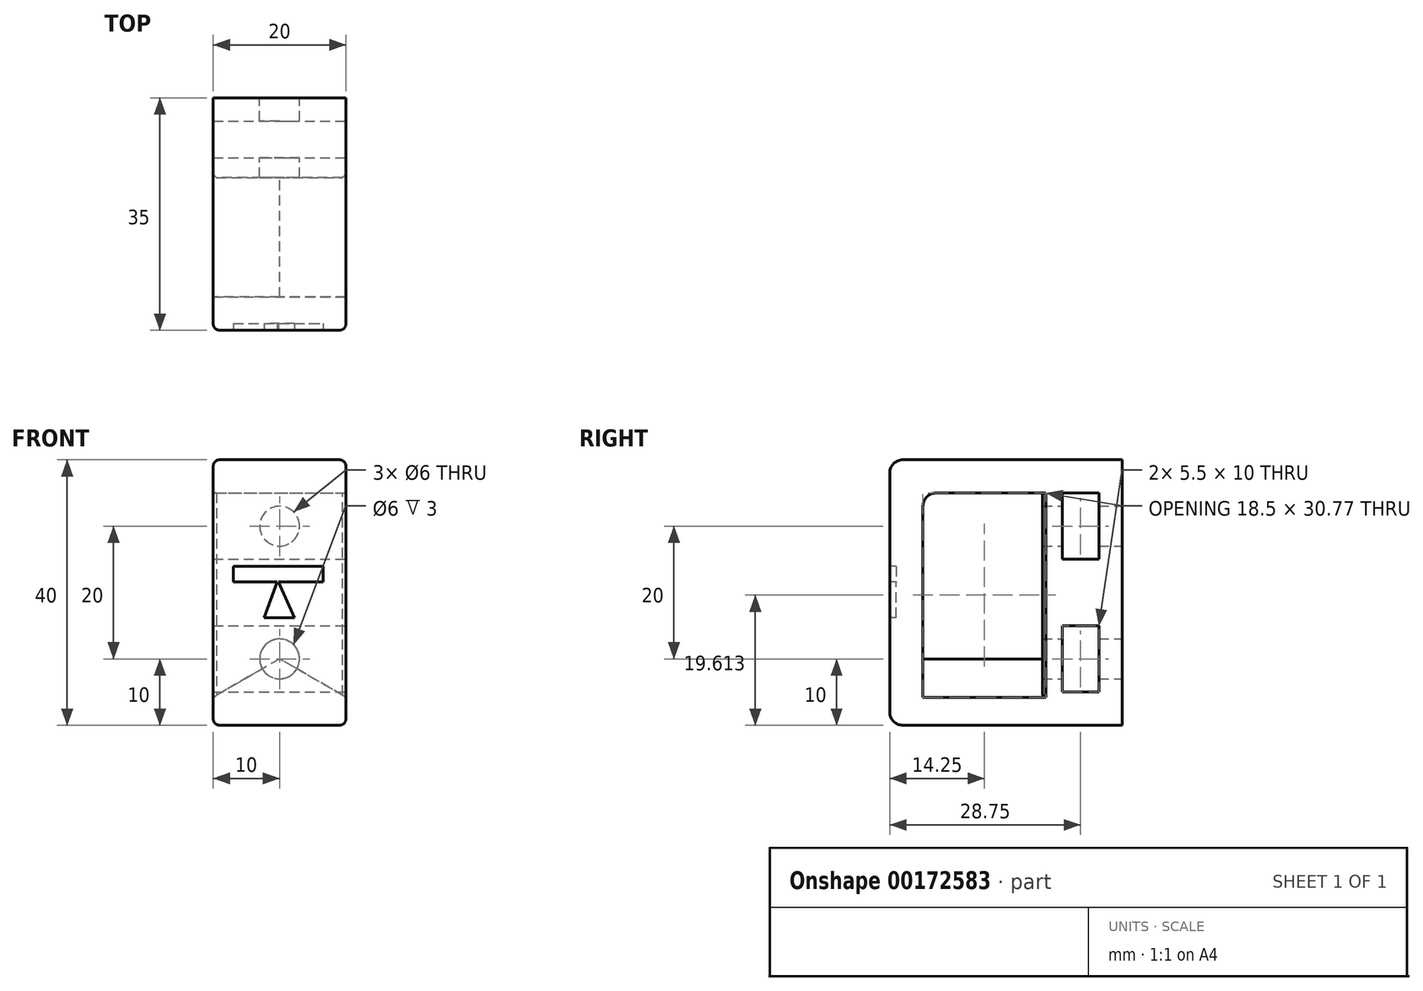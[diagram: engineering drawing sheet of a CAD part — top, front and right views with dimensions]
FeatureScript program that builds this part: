
annotation { "Feature Type Name" : "Feature", "Feature Type Description" : "" }
export const myFeature = defineFeature(function(context is Context, id is Id, definition is map)
    precondition{}
    {
        {
            var Q0;
            Q0=qCreatedBy(makeId("Front.planeOp"),FACE);
            var sketch = newSketch(context, id + "F0", { "sketchPlane" : qUnion([Q0])});
            skLineSegment(sketch, "E0.bottom", {"start": v(0, 0) * mm, "end": v(20, 0) * mm});
            skLineSegment(sketch, "E0.top", {"start": v(0, 40) * mm, "end": v(20, 40) * mm});
            skLineSegment(sketch, "E0.left", {"start": v(0, 0) * mm, "end": v(0, 40) * mm});
            skLineSegment(sketch, "E0.right", {"start": v(20, 0) * mm, "end": v(20, 40) * mm});
            skSolve(sketch);
        }
        {
            var Q0;
            Q0=qSketchRegion(id+"F0",true);
            extrude(context, id + "F1", {"entities" : qUnion([Q0]), "depth" : 12 * mm});
        }
        {
            var Q0;
            Q0=makeQuery(id+"F1.opExtrude","CAP_FACE",FACE,{"disambiguationData":[OSD([sQuery(id+"F0.wireOp",EDGE,"E0.bottom"),sQuery(id+"F0.wireOp",EDGE,"E0.top"),sQuery(id+"F0.wireOp",EDGE,"E0.left"),sQuery(id+"F0.wireOp",EDGE,"E0.right")])],"isStart":true});
            var sketch = newSketch(context, id + "F2", { "sketchPlane" : qUnion([Q0])});
            skCircle(sketch, "E1", {"center": v(-10, 30) * mm, "radius": 3 * mm});
            skPoint(sketch, "E1.centerSnap0", {"position": v(-10, 40) * mm});
            skCircle(sketch, "E2", {"center": v(-10, 10) * mm, "radius": 3 * mm});
            skSolve(sketch);
        }
        {
            var Q0;
            Q0=qSketchRegion(id+"F2",true);
            var Q1;
            Q1=makeQuery(id+"F1.opExtrude","CAP_FACE",FACE,{"disambiguationData":[OSD([sQuery(id+"F0.wireOp",EDGE,"E0.bottom"),sQuery(id+"F0.wireOp",EDGE,"E0.top"),sQuery(id+"F0.wireOp",EDGE,"E0.left"),sQuery(id+"F0.wireOp",EDGE,"E0.right")])],"isStart":false});
            extrude(context, id + "F3", {"entities" : qUnion([Q0]), "operationType" : NewBodyOperationType.REMOVE, "endBound" : BoundingType.UP_TO_SURFACE, "oppositeDirection" : true, "endBoundEntityFace" : qUnion([Q1]), "depth" : 25 * mm});
        }
        {
            var Q0;
            Q0=makeQuery(id+"F1.opExtrude","CAP_FACE",FACE,{"disambiguationData":[OSD([sQuery(id+"F0.wireOp",EDGE,"E0.bottom"),sQuery(id+"F0.wireOp",EDGE,"E0.top"),sQuery(id+"F0.wireOp",EDGE,"E0.left"),sQuery(id+"F0.wireOp",EDGE,"E0.right")])],"isStart":false});
            var sketch = newSketch(context, id + "F4", { "sketchPlane" : qUnion([Q0])});
            skLineSegment(sketch, "E3", {"start": v(0, 0) * mm, "end": v(20, 0) * mm});
            skLineSegment(sketch, "E4", {"start": v(20, 0) * mm, "end": v(20, 4.23) * mm});
            skLineSegment(sketch, "E5", {"start": v(20, 4.23) * mm, "end": v(10, 10) * mm});
            skPoint(sketch, "E5.endSnap0", {"position": v(10, 0) * mm});
            skLineSegment(sketch, "E6", {"start": v(10, 10) * mm, "end": v(0, 4.23) * mm});
            skLineSegment(sketch, "E7", {"start": v(0, 4.23) * mm, "end": v(0, 0) * mm});
            skSolve(sketch);
        }
        {
            var Q0;
            Q0 = qSketchRegion(id + "F4", true);
            extrude(context, id + "F5", {"entities" : qUnion([Q0]), "operationType" : NewBodyOperationType.ADD, "depth" : 23 * mm});
        }
        {
            var Q0;
            Q0=makeQuery(id+"F5.boolean.opBoolean","MERGE",FACE,{"derivedFrom":[makeQuery(id+"F1.opExtrude","SWEPT_FACE",FACE,{"disambiguationData":[OSD([sQuery(id+"F0.wireOp",EDGE,"E0.right")])]}),makeQuery(id+"F5.opExtrude","SWEPT_FACE",FACE,{"disambiguationData":[OSD([sQuery(id+"F4.wireOp",EDGE,"E4")])]})]});
            var sketch = newSketch(context, id + "F6", { "sketchPlane" : qUnion([Q0])});
            skLineSegment(sketch, "E8", {"start": v(-35, 0) * mm, "end": v(-35, 40) * mm});
            skLineSegment(sketch, "E9", {"start": v(-35, 40) * mm, "end": v(-12, 40) * mm});
            skLineSegment(sketch, "E10", {"start": v(-12, 40) * mm, "end": v(-12, 35) * mm});
            skLineSegment(sketch, "E11", {"start": v(-12, 35) * mm, "end": v(-30, 35) * mm});
            skLineSegment(sketch, "E12", {"start": v(-30, 35) * mm, "end": v(-30, 0) * mm});
            skLineSegment(sketch, "E13", {"start": v(-30, 0) * mm, "end": v(-35, 0) * mm});
            skSolve(sketch);
        }
        {
            var Q0;
            {var subQ1=sQuery(id+"F6.wireOp",EDGE,"E9");Q0=makeQuery(id+"F6.imprint","IMPRINT",FACE,{"disambiguationData":[TD([[makeQuery(id+"F6.imprint","IMPRINT",EDGE,{"derivedFrom":subQ1}),-1.0]])]});}
            var Q1;
            Q1=makeQuery(id+"F5.boolean.opBoolean","MERGE",FACE,{"derivedFrom":[makeQuery(id+"F1.opExtrude","SWEPT_FACE",FACE,{"disambiguationData":[OSD([sQuery(id+"F0.wireOp",EDGE,"E0.left")])]}),makeQuery(id+"F5.opExtrude","SWEPT_FACE",FACE,{"disambiguationData":[OSD([sQuery(id+"F4.wireOp",EDGE,"E7")])]})]});
            extrude(context, id + "F7", {"entities" : qUnion([Q0]), "operationType" : NewBodyOperationType.ADD, "endBound" : BoundingType.UP_TO_SURFACE, "oppositeDirection" : true, "endBoundEntityFace" : qUnion([Q1]), "depth" : 25 * mm});
        }
        {
            var Q0;
            Q0=makeQuery(id+"F7.opExtrude","SWEPT_EDGE",EDGE,{"disambiguationData":[OSD([sQuery(id+"F6.wireOp",EDGE,"E8"),sQuery(id+"F6.wireOp",EDGE,"E9")])]});
            var Q1;
            Q1=makeQuery(id+"F5.opExtrude","CAP_EDGE",EDGE,{"disambiguationData":[OSD([sQuery(id+"F4.wireOp",EDGE,"E3")])],"isStart":false});
            var Q2;
            Q2=makeQuery(id+"F7.opExtrude","SWEPT_EDGE",EDGE,{"disambiguationData":[OSD([sQuery(id+"F6.wireOp",EDGE,"E11"),sQuery(id+"F6.wireOp",EDGE,"E12")])]});
            var Q3;
            Q3=makeQuery(id+"F7.opExtrude","SWEPT_EDGE",EDGE,{"disambiguationData":[OSD([sQuery(id+"F0.wireOp",EDGE,"E0.right"),sQuery(id+"F6.wireOp",EDGE,"E10"),sQuery(id+"F6.wireOp",EDGE,"E11")])]});
            fillet(context, id + "F8", {"entities" : qUnion([Q0, Q1, Q2, Q3]), "radius" : 2 * mm, "tangentPropagation" : true, "allowEdgeOverflow" : false});
        }
        {
            var Q0;
            Q0=makeQuery(id+"F7.boolean.opBoolean","MERGE",EDGE,{"derivedFrom":[makeQuery(id+"F5.opExtrude","CAP_EDGE",EDGE,{"disambiguationData":[OSD([sQuery(id+"F4.wireOp",EDGE,"E4")])],"isStart":false}),makeQuery(id+"F7.opExtrude","CAP_EDGE",EDGE,{"disambiguationData":[OSD([sQuery(id+"F6.wireOp",EDGE,"E8")])],"isStart":true})]});
            var Q1;
            {var subQ0=sQuery(id+"F6.wireOp",EDGE,"E8");var subQ1=sQuery(id+"F4.wireOp",EDGE,"E7");Q1=makeQuery(id+"F7.boolean.opBoolean","MERGE",EDGE,{"derivedFrom":[makeQuery(id+"F5.opExtrude","CAP_EDGE",EDGE,{"disambiguationData":[OSD([subQ1])],"isStart":false}),makeQuery(id+"F7.opExtrude","TWEAK_EDGE",EDGE,{"derivedFrom":[makeQuery(id+"F5.boolean.opBoolean","MERGE",FACE,{"derivedFrom":[makeQuery(id+"F1.opExtrude","SWEPT_FACE",FACE,{"disambiguationData":[OSD([sQuery(id+"F0.wireOp",EDGE,"E0.left")])]}),makeQuery(id+"F5.opExtrude","SWEPT_FACE",FACE,{"disambiguationData":[OSD([subQ1])]})]}),makeQuery(id+"F6.imprint","IMPRINT",EDGE,{"disambiguationData":[TD([[makeQuery(id+"F6.imprint","INTERSECT",VERTEX,{"derivedFrom":[subQ0,sQuery(id+"F6.wireOp",EDGE,"E9")]}),1.0]])],"derivedFrom":subQ0})]})]});}
            fillet(context, id + "F9", {"entities" : qUnion([Q0, Q1]), "radius" : 1 * mm, "tangentPropagation" : true, "allowEdgeOverflow" : false});
        }
        {
            var Q0;
            {var subQ0=sQuery(id+"F4.wireOp",EDGE,"E4");var subQ1=sQuery(id+"F0.wireOp",EDGE,"E0.right");Q0=makeQuery(id+"F7.boolean.opBoolean","MERGE",FACE,{"derivedFrom":[makeQuery(id+"F5.boolean.opBoolean","MERGE",FACE,{"derivedFrom":[makeQuery(id+"F1.opExtrude","SWEPT_FACE",FACE,{"disambiguationData":[OSD([subQ1])]}),makeQuery(id+"F5.opExtrude","SWEPT_FACE",FACE,{"disambiguationData":[OSD([subQ0])]})]}),makeQuery(id+"F7.opExtrude","CAP_FACE",FACE,{"disambiguationData":[OSD([subQ1,subQ0,sQuery(id+"F4.wireOp",EDGE,"E5"),sQuery(id+"F6.wireOp",EDGE,"E8"),sQuery(id+"F6.wireOp",EDGE,"E9"),sQuery(id+"F6.wireOp",EDGE,"E10"),sQuery(id+"F6.wireOp",EDGE,"E11"),sQuery(id+"F6.wireOp",EDGE,"E12")])],"isStart":true})]});}
            var sketch = newSketch(context, id + "F10", { "sketchPlane" : qUnion([Q0])});
            skLineSegment(sketch, "E14.bottom", {"start": v(-9, 35) * mm, "end": v(-3.5, 35) * mm});
            skLineSegment(sketch, "E14.top", {"start": v(-9, 25) * mm, "end": v(-3.5, 25) * mm});
            skLineSegment(sketch, "E14.left", {"start": v(-9, 35) * mm, "end": v(-9, 25) * mm});
            skLineSegment(sketch, "E14.right", {"start": v(-3.5, 35) * mm, "end": v(-3.5, 25) * mm});
            skLineSegment(sketch, "E15.bottom", {"start": v(-9, 15) * mm, "end": v(-3.5, 15) * mm});
            skLineSegment(sketch, "E15.top", {"start": v(-9, 5) * mm, "end": v(-3.5, 5) * mm});
            skLineSegment(sketch, "E15.left", {"start": v(-9, 15) * mm, "end": v(-9, 5) * mm});
            skLineSegment(sketch, "E15.right", {"start": v(-3.5, 15) * mm, "end": v(-3.5, 5) * mm});
            skSolve(sketch);
        }
        {
            var Q0;
            Q0 = qSketchRegion(id + "F10", true);
            extrude(context, id + "F11", {"entities" : qUnion([Q0]), "operationType" : NewBodyOperationType.REMOVE, "oppositeDirection" : true, "depth" : 25 * mm});
        }
        {
            var Q0;
            Q0=makeQuery(id+"F7.boolean.opBoolean","MERGE",FACE,{"derivedFrom":[makeQuery(id+"F5.opExtrude","CAP_FACE",FACE,{"disambiguationData":[OSD([sQuery(id+"F4.wireOp",EDGE,"E3"),sQuery(id+"F4.wireOp",EDGE,"E4"),sQuery(id+"F4.wireOp",EDGE,"E5"),sQuery(id+"F4.wireOp",EDGE,"E6"),sQuery(id+"F4.wireOp",EDGE,"E7")])],"isStart":false}),makeQuery(id+"F7.opExtrude","SWEPT_FACE",FACE,{"disambiguationData":[OSD([sQuery(id+"F6.wireOp",EDGE,"E8")])]})]});
            var sketch = newSketch(context, id + "F12", { "sketchPlane" : qUnion([Q0])});
            skLineSegment(sketch, "E16.bottom", {"start": v(3.04, 23.95) * mm, "end": v(16.59, 23.95) * mm});
            skLineSegment(sketch, "E16.top", {"start": v(3.04, 21.57) * mm, "end": v(16.59, 21.57) * mm});
            skLineSegment(sketch, "E16.left", {"start": v(3.04, 23.95) * mm, "end": v(3.04, 21.57) * mm});
            skLineSegment(sketch, "E16.right", {"start": v(16.59, 23.95) * mm, "end": v(16.59, 21.57) * mm});
            skLineSegment(sketch, "E17", {"start": v(9.81, 21.57) * mm, "end": v(12.27, 16.2) * mm});
            skLineSegment(sketch, "E18", {"start": v(12.27, 16.2) * mm, "end": v(7.65, 16.2) * mm});
            skLineSegment(sketch, "E19", {"start": v(7.65, 16.2) * mm, "end": v(9.65, 21.57) * mm});
            skSolve(sketch);
        }
        {
            var Q0;
            Q0 = qSketchRegion(id + "F12", true);
            extrude(context, id + "F13", {"entities" : qUnion([Q0]), "operationType" : NewBodyOperationType.REMOVE, "oppositeDirection" : true, "depth" : 1 * mm});
        }
        {
            var Q0;
            Q0=makeQuery(id+"F1.opExtrude","CAP_EDGE",EDGE,{"disambiguationData":[OSD([sQuery(id+"F0.wireOp",EDGE,"E0.right")])],"isStart":false});
            var Q1;
            Q1=makeQuery(id+"F1.opExtrude","CAP_EDGE",EDGE,{"disambiguationData":[OSD([sQuery(id+"F0.wireOp",EDGE,"E0.left")])],"isStart":false});
            chamfer(context, id + "F14", {"entities" : qUnion([Q0, Q1]), "width" : 0.5 * mm, "tangentPropagation" : true});
        }
    });
